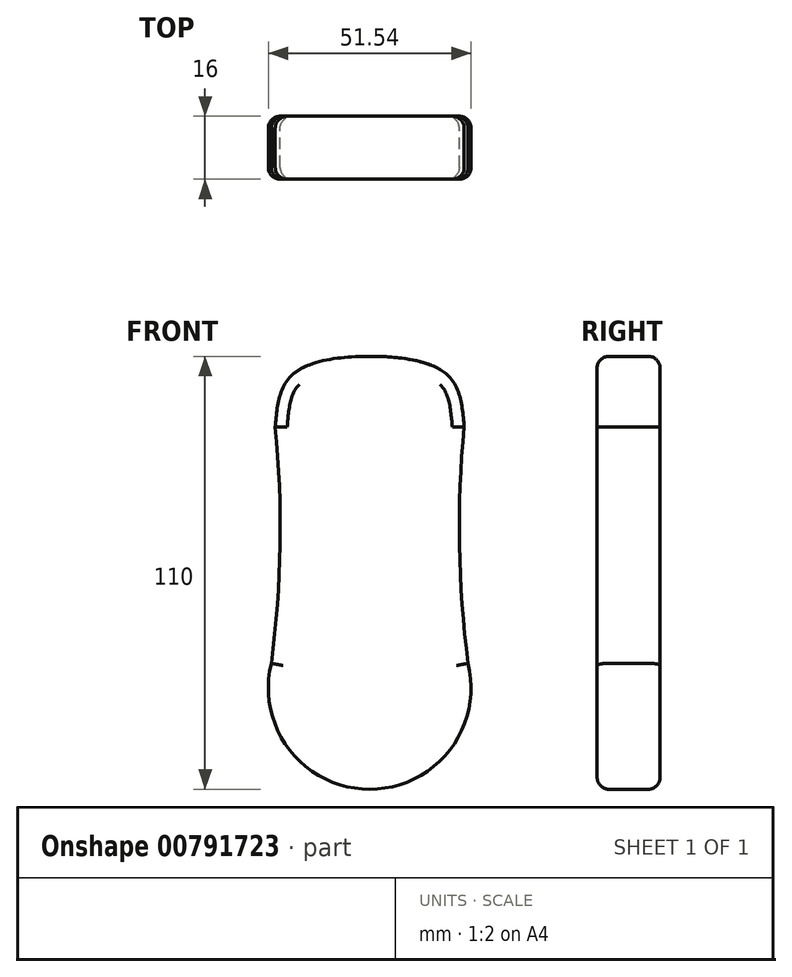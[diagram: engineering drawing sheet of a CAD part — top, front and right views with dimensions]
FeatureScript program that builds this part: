
annotation { "Feature Type Name" : "Feature", "Feature Type Description" : "" }
export const myFeature = defineFeature(function(context is Context, id is Id, definition is map)
    precondition{}
    {
        {
            var Q0;
            Q0=qCreatedBy(makeId("Front.planeOp"),FACE);
            var sketch = newSketch(context, id + "F0", { "sketchPlane" : qUnion([Q0])});
            skLineSegment(sketch, "E0.bottom", {"start": v(0, 0) * mm, "end": v(50, 0) * mm, "construction": true});
            skLineSegment(sketch, "E0.top", {"start": v(0, 110) * mm, "end": v(50, 110) * mm, "construction": true});
            skLineSegment(sketch, "E0.left", {"start": v(0, 0) * mm, "end": v(0, 110) * mm, "construction": true});
            skLineSegment(sketch, "E0.right", {"start": v(50, 0) * mm, "end": v(50, 110) * mm, "construction": true});
            skLineSegment(sketch, "E1", {"start": v(25, 0) * mm, "end": v(25, 32) * mm, "construction": true});
            skLineSegment(sketch, "E2", {"start": v(0, 32) * mm, "end": v(50, 32) * mm, "construction": true});
            skArc(sketch, "E3", {"start": v(0, 32) * mm, "mid": v(25, 0) * mm, "end": v(50, 32) * mm});
            skLineSegment(sketch, "E4", {"start": v(25, 110) * mm, "end": v(25, 92) * mm});
            skLineSegment(sketch, "E5", {"start": v(1, 92) * mm, "end": v(49, 92) * mm});
            skLineSegment(sketch, "E6", {"start": v(5, 105) * mm, "end": v(45, 105) * mm});
            skPoint(sketch, "E7", {"position": v(25, 105) * mm});
            skFitSpline(sketch, "E8", {"points": [v(1, 92) * mm, v(5, 105) * mm, v(25, 110) * mm, v(45, 105) * mm, v(49, 92) * mm], "startDerivative": vector(5.6, 66.02) * mm, "endDerivative": vector(5.6, -66.02) * mm});
            skLineSegment(sketch, "E9", {"start": v(2, 55) * mm, "end": v(48, 55) * mm, "construction": true});
            skLineSegment(sketch, "E10", {"start": v(25, 32) * mm, "end": v(25, 55) * mm, "construction": true});
            skArc(sketch, "E11", {"start": v(0, 32) * mm, "mid": v(2.2, 61.97) * mm, "end": v(1, 92) * mm});
            skArc(sketch, "E12", {"start": v(49, 92) * mm, "mid": v(47.8, 61.97) * mm, "end": v(50, 32) * mm});
            skSolve(sketch);
        }
        {
            var Q0;
            Q0 = qSketchRegion(id + "F0", true);
            extrude(context, id + "F1", {"entities" : qUnion([Q0]), "depth" : 16 * mm, "offsetDistance" : 25 * mm});
        }
        {
            var Q0;
            Q0=makeQuery(id+"F1.opExtrude","CAP_FACE",FACE,{"disambiguationData":[OSD([sQuery(id+"F0.wireOp",EDGE,"E3"),sQuery(id+"F0.wireOp",EDGE,"E8"),sQuery(id+"F0.wireOp",EDGE,"E11"),sQuery(id+"F0.wireOp",EDGE,"E12")])],"isStart":false});
            fillet(context, id + "F2", {"entities" : qUnion([Q0]), "radius" : 3 * mm, "tangentPropagation" : true, "allowEdgeOverflow" : false});
        }
        {
            var Q0;
            Q0=makeQuery(id+"F1.opExtrude","CAP_FACE",FACE,{"disambiguationData":[OSD([sQuery(id+"F0.wireOp",EDGE,"E3"),sQuery(id+"F0.wireOp",EDGE,"E8"),sQuery(id+"F0.wireOp",EDGE,"E11"),sQuery(id+"F0.wireOp",EDGE,"E12")])],"isStart":true});
            fillet(context, id + "F3", {"entities" : qUnion([Q0]), "radius" : 3 * mm, "tangentPropagation" : true, "allowEdgeOverflow" : false});
        }
    });
